# Revit family: SanitaryEquipment_Lovair_IR-sensor-tap_TSL-882
name_source: partatom
category: Furniture
revit_build: Autodesk Revit 2016 (Build: 20160314_0715(x64)
units: mm (PartAtom-declared; Revit-internal decimal feet)

## family parameters
Cut with Voids When Loaded = No
Host = Face
OmniClass Number = 23.45.05.14.14
OmniClass Title = Sinks/Lavatories
Room Calculation Point = No
Shared = No

## types (5) — shared parameters
Assembly Code = D2010400
AssetType = Fixed
BIMObjectName = SanitaryEquipment_Lovair_IR-sensor-tap_TSL-882
Category = Pr_40_20_87_98
Default Elevation = 1219.2 mm  [stored 4 ft]
DurationUnit = Year
Manufacturer = TheSplashLab
ManufacturerName = TheSplashLab
ManufacturerURL = https://thesplashlab.com
Model = TSL-882
NBSReference = Pr_40_20_87_98
Name = SanitaryEquipment_Lovair_IR-sensor-tap_TSL-882
NominalHeight = 220 mm  [stored 0.721785 ft]
NominalLength = 45 mm  [stored 0.147638 ft]
NominalWidth = 16.3 mm
Revision = 0
URL = https://thesplashlab.com
Uniclass2015Code = Pr_40_20_87_98
Uniclass2015Title = Washbasin taps
Uniclass2015Version = UK_NBS_Uniclass2015_04_18
Version = 1
WarrantyDurationUnit = Year

## per-type parameters (varying)
| type | HousingMaterial |
| Bronze | Brushed Bronze |
| Copper | Brushed Copper |
| Black | Brushed Black |
| Brass | Brushed Brass |
| Satin | Stainless Steel |

note: [stored X ft] marks values corroborated as IEEE doubles in the binary element streams (Revit-internal decimal feet)

## geometry (parser evidence)
native form markers: Sweep x2
no freeform markers — native parametric forms only
